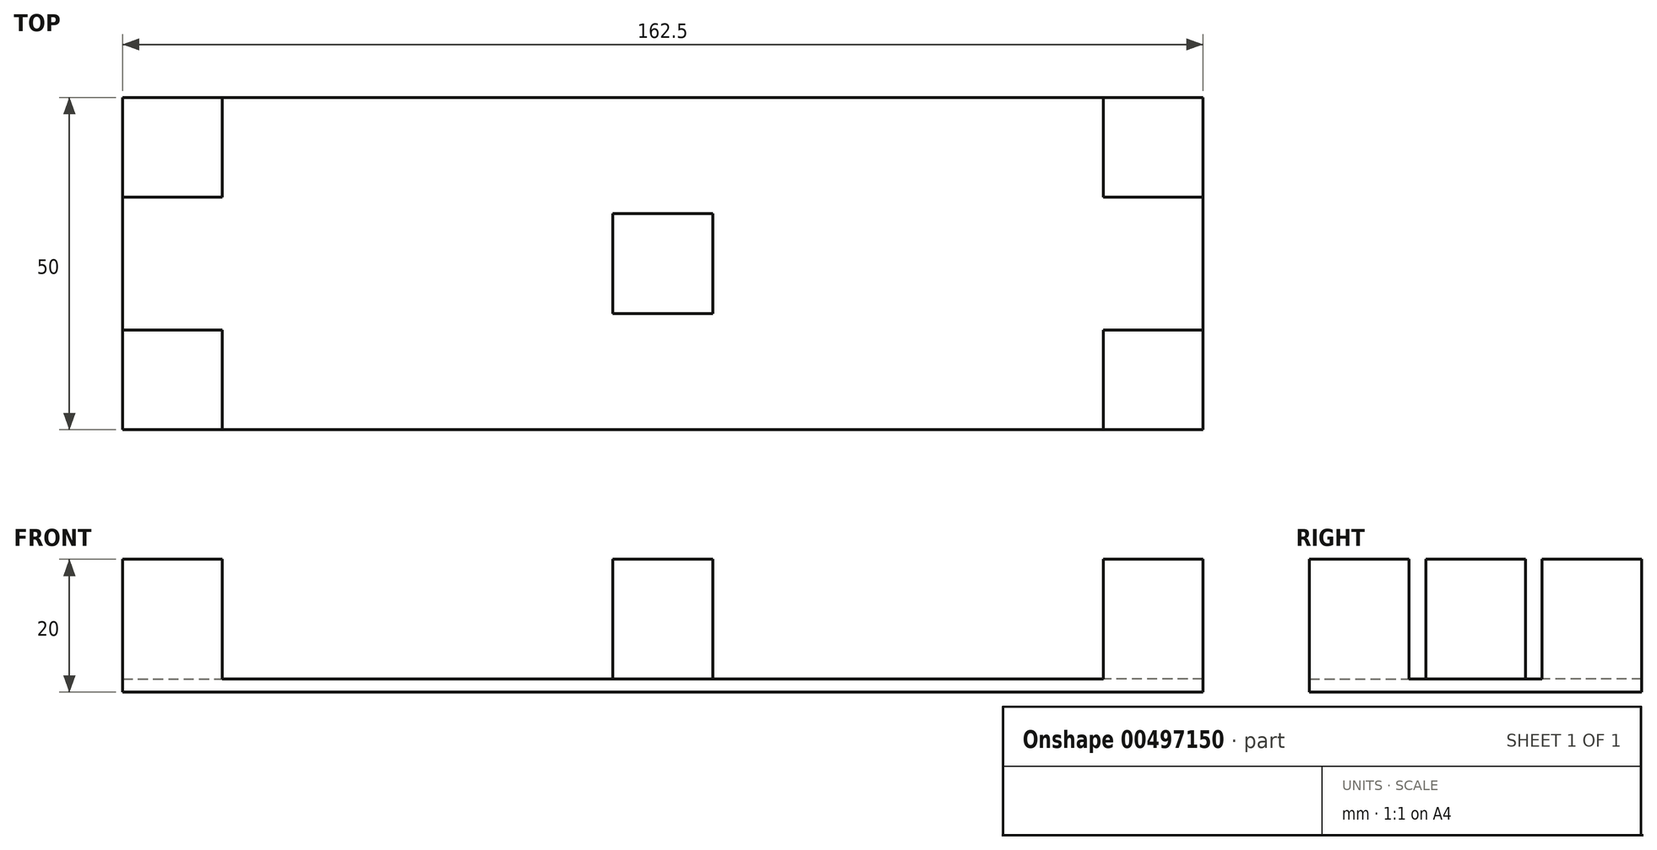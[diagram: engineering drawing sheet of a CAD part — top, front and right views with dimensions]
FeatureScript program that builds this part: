
annotation { "Feature Type Name" : "Feature", "Feature Type Description" : "" }
export const myFeature = defineFeature(function(context is Context, id is Id, definition is map)
    precondition{}
    {
        {
            var Q0;
            Q0=qCreatedBy(makeId("Top.planeOp"),FACE);
            var sketch = newSketch(context, id + "F0", { "sketchPlane" : qUnion([Q0])});
            skLineSegment(sketch, "E0.bottom", {"start": v(-81.25, 25) * mm, "end": v(81.25, 25) * mm});
            skLineSegment(sketch, "E0.top", {"start": v(-81.25, -25) * mm, "end": v(81.25, -25) * mm});
            skLineSegment(sketch, "E0.left", {"start": v(-81.25, 25) * mm, "end": v(-81.25, -25) * mm});
            skLineSegment(sketch, "E0.right", {"start": v(81.25, 25) * mm, "end": v(81.25, -25) * mm});
            skPoint(sketch, "E0.middle", {"position": v(0, 0) * mm});
            skSolve(sketch);
        }
        {
            var Q0;
            Q0 = qSketchRegion(id + "F0", true);
            extrude(context, id + "F1", {"entities" : qUnion([Q0]), "depth" : 2 * mm});
        }
        {
            var Q0;
            Q0=makeQuery(id+"F1.opExtrude","CAP_FACE",FACE,{"disambiguationData":[OSD([sQuery(id+"F0.wireOp",EDGE,"E0.bottom"),sQuery(id+"F0.wireOp",EDGE,"E0.top"),sQuery(id+"F0.wireOp",EDGE,"E0.left"),sQuery(id+"F0.wireOp",EDGE,"E0.right")])],"isStart":false});
            var sketch = newSketch(context, id + "F2", { "sketchPlane" : qUnion([Q0])});
            skLineSegment(sketch, "E1.bottom", {"start": v(-81.25, -25) * mm, "end": v(-66.25, -25) * mm});
            skLineSegment(sketch, "E1.top", {"start": v(-81.25, -10) * mm, "end": v(-66.25, -10) * mm});
            skLineSegment(sketch, "E1.left", {"start": v(-81.25, -25) * mm, "end": v(-81.25, -10) * mm});
            skLineSegment(sketch, "E1.right", {"start": v(-66.25, -25) * mm, "end": v(-66.25, -10) * mm});
            skLineSegment(sketch, "E2.bottom", {"start": v(-81.25, 25) * mm, "end": v(-66.25, 25) * mm});
            skLineSegment(sketch, "E2.top", {"start": v(-81.25, 10) * mm, "end": v(-66.25, 10) * mm});
            skLineSegment(sketch, "E2.left", {"start": v(-81.25, 25) * mm, "end": v(-81.25, 10) * mm});
            skLineSegment(sketch, "E2.right", {"start": v(-66.25, 25) * mm, "end": v(-66.25, 10) * mm});
            skLineSegment(sketch, "E3.bottom", {"start": v(81.25, 25) * mm, "end": v(66.25, 25) * mm});
            skLineSegment(sketch, "E3.top", {"start": v(81.25, 10) * mm, "end": v(66.25, 10) * mm});
            skLineSegment(sketch, "E3.left", {"start": v(81.25, 25) * mm, "end": v(81.25, 10) * mm});
            skLineSegment(sketch, "E3.right", {"start": v(66.25, 25) * mm, "end": v(66.25, 10) * mm});
            skLineSegment(sketch, "E4.bottom", {"start": v(81.25, -25) * mm, "end": v(66.25, -25) * mm});
            skLineSegment(sketch, "E4.top", {"start": v(81.25, -10) * mm, "end": v(66.25, -10) * mm});
            skLineSegment(sketch, "E4.left", {"start": v(81.25, -25) * mm, "end": v(81.25, -10) * mm});
            skLineSegment(sketch, "E4.right", {"start": v(66.25, -25) * mm, "end": v(66.25, -10) * mm});
            skLineSegment(sketch, "E5.bottom", {"start": v(7.5, 7.5) * mm, "end": v(-7.5, 7.5) * mm});
            skLineSegment(sketch, "E5.top", {"start": v(7.5, -7.5) * mm, "end": v(-7.5, -7.5) * mm});
            skLineSegment(sketch, "E5.left", {"start": v(7.5, 7.5) * mm, "end": v(7.5, -7.5) * mm});
            skLineSegment(sketch, "E5.right", {"start": v(-7.5, 7.5) * mm, "end": v(-7.5, -7.5) * mm});
            skPoint(sketch, "E5.middle", {"position": v(0, 0) * mm});
            skSolve(sketch);
        }
        {
            var Q0;
            Q0 = qSketchRegion(id + "F2", true);
            extrude(context, id + "F3", {"entities" : qUnion([Q0]), "operationType" : NewBodyOperationType.ADD, "depth" : 18 * mm});
        }
    });
